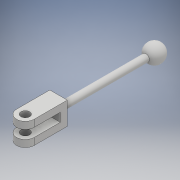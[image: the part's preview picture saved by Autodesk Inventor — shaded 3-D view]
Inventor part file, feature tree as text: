
AUTODESK INVENTOR PART (.ipt)
format: ipt  version: 2018 (Build 220112000, 112)  size: 147,968 bytes
history: native  units: mm
features: sketch x3, extrude x2, revolve x1, fillet x1, hole x1
ambient origin geometry x8: Origin, YZ Plane, XZ Plane, XY Plane, X Axis, Y Axis, Z Axis, Center Point
bodies: Solid1 (feature_tree)
feature tree (8):
  extrude  "Extrusion1"  Depth=4.0mm
  extrude  "Extrusion2"  Depth=5.0mm
  revolve  "Revolution1"  [1 undecoded]
  fillet  "Fillet1"  Radius=5.0mm
  hole  "Hole1"  [1 undecoded]
  sketch  "Sketch1"  dims[d0=4.0mm d1=20.0mm]
  sketch  "Sketch2"  dims[d2=4.0mm d3=5.0mm]
  sketch  "Sketch3"  dims[d4=10.0mm d5=0.0mm d6=4.0mm d7=5.0mm d8=6.5mm d9=50.0mm d10=0.0mm d11=2.5mm d12=0.0mm d13=10.0mm d14=90.0deg d15=5.0mm d16=10.0mm d17=10.0mm d18=5.0mm d19=6.0mm d20=4.0mm d21=2.0mm d22=90.0deg d23=8.0mm d24=0.0mm]
note: 2 required parameter values undecoded (feature->parameter linkage not recoverable at this tier; creation-order binding heuristic only, values carry confidence <= 0.55)